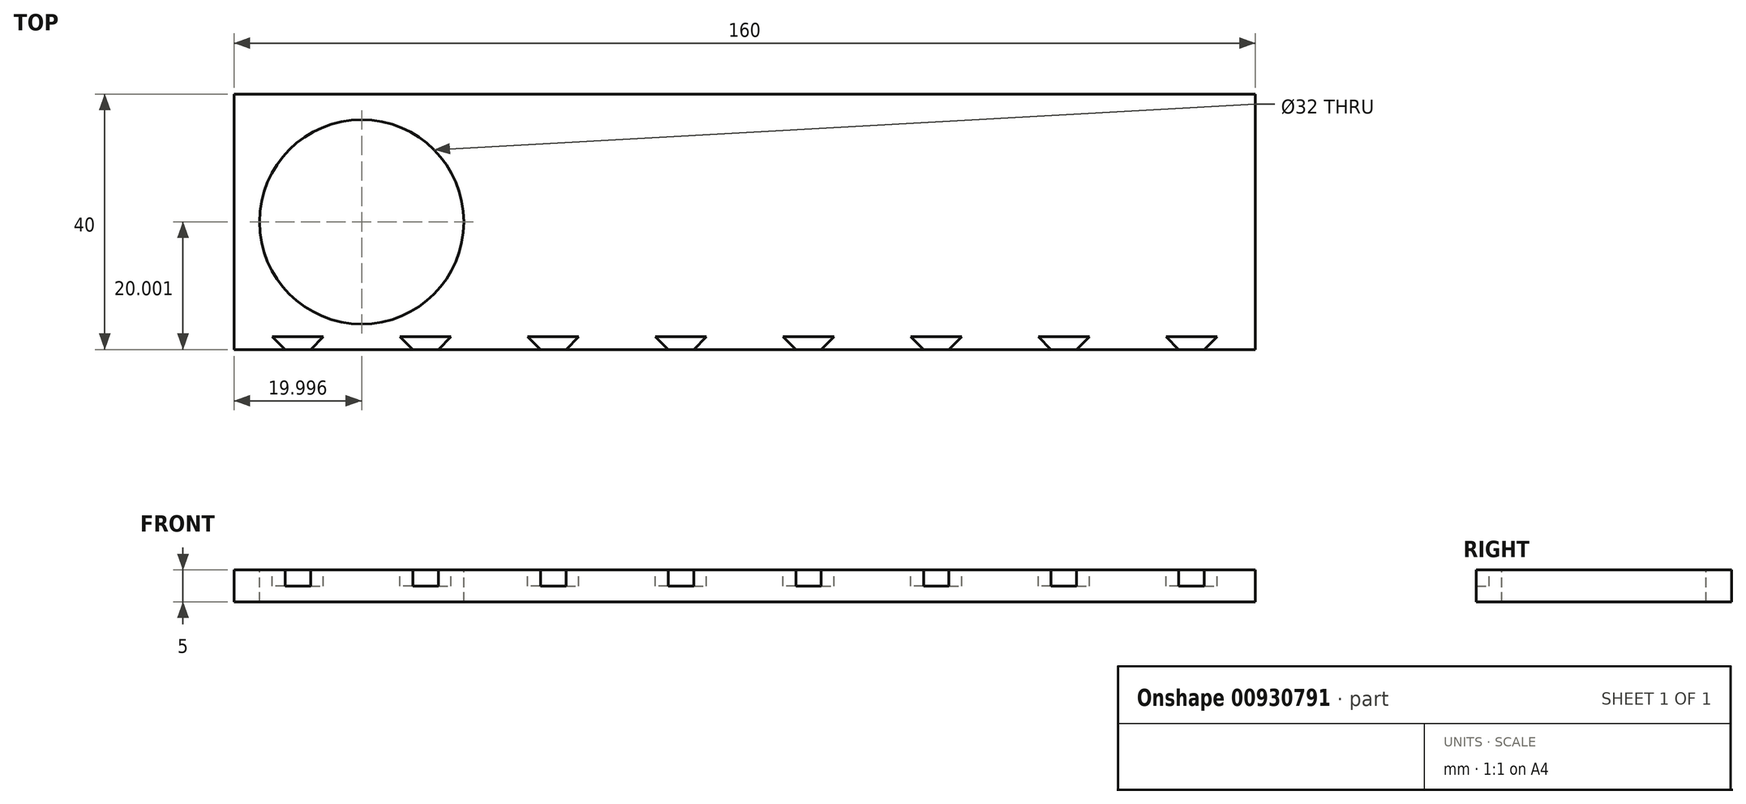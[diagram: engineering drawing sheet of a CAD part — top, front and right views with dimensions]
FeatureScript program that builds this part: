
annotation { "Feature Type Name" : "Feature", "Feature Type Description" : "" }
export const myFeature = defineFeature(function(context is Context, id is Id, definition is map)
    precondition{}
    {
        {
            var Q0;
            Q0=qCreatedBy(makeId("Top.planeOp"),FACE);
            var sketch = newSketch(context, id + "F0", { "sketchPlane" : qUnion([Q0])});
            skLineSegment(sketch, "E0.bottom", {"start": v(-67.6, 58.98) * mm, "end": v(92.4, 58.98) * mm});
            skLineSegment(sketch, "E0.top", {"start": v(-67.6, 18.98) * mm, "end": v(92.4, 18.98) * mm});
            skLineSegment(sketch, "E0.left", {"start": v(-67.6, 58.98) * mm, "end": v(-67.6, 18.98) * mm});
            skLineSegment(sketch, "E0.right", {"start": v(92.4, 58.98) * mm, "end": v(92.4, 18.98) * mm});
            skSolve(sketch);
        }
        {
            var Q0;
            Q0=makeQuery(id+"F0.imprint","IMPRINT",FACE,{"disambiguationData":[TD([[makeQuery(id+"F0.imprint","IMPRINT",EDGE,{"derivedFrom":sQuery(id+"F0.wireOp",EDGE,"E0.bottom")}),-1.0]])]});
            extrude(context, id + "F1", {"entities" : qUnion([Q0]), "depth" : 5 * mm, "offsetDistance" : 25 * mm});
        }
        {
            var Q0;
            Q0=makeQuery(id+"F1.opExtrude","CAP_FACE",FACE,{"disambiguationData":[OSD([sQuery(id+"F0.wireOp",EDGE,"E0.bottom"),sQuery(id+"F0.wireOp",EDGE,"E0.top"),sQuery(id+"F0.wireOp",EDGE,"E0.left"),sQuery(id+"F0.wireOp",EDGE,"E0.right")])],"isStart":false});
            var sketch = newSketch(context, id + "F2", { "sketchPlane" : qUnion([Q0])});
            skCircle(sketch, "E1", {"center": v(-47.6, 38.98) * mm, "radius": 16 * mm});
            skPoint(sketch, "E1.centerSnap0", {"position": v(-67.6, 38.98) * mm});
            skSolve(sketch);
        }
        {
            var Q0;
            Q0=makeQuery(id+"F2.imprint","IMPRINT",FACE,{"disambiguationData":[TD([[makeQuery(id+"F2.imprint","IMPRINT",EDGE,{"derivedFrom":sQuery(id+"F2.wireOp",EDGE,"E1")}),1.0]])]});
            extrude(context, id + "F3", {"entities" : qUnion([Q0]), "operationType" : NewBodyOperationType.REMOVE, "oppositeDirection" : true, "depth" : 5 * mm, "offsetDistance" : 25 * mm});
        }
        {
            var Q0;
            Q0=makeQuery(id+"F1.opExtrude","CAP_FACE",FACE,{"disambiguationData":[OSD([sQuery(id+"F0.wireOp",EDGE,"E0.bottom"),sQuery(id+"F0.wireOp",EDGE,"E0.top"),sQuery(id+"F0.wireOp",EDGE,"E0.left"),sQuery(id+"F0.wireOp",EDGE,"E0.right")])],"isStart":false});
            var sketch = newSketch(context, id + "F4", { "sketchPlane" : qUnion([Q0])});
            skLineSegment(sketch, "E2", {"start": v(-67.6, 20.98) * mm, "end": v(92.4, 20.98) * mm});
            skPoint(sketch, "E3", {"position": v(-57.6, 18.98) * mm});
            skLineSegment(sketch, "E4", {"start": v(-59.6, 18.98) * mm, "end": v(-61.6, 20.98) * mm});
            skLineSegment(sketch, "E5", {"start": v(-55.6, 18.98) * mm, "end": v(-53.6, 20.98) * mm});
            skLineSegment(sketch, "E6.1.0.0", {"start": v(-39.6, 18.98) * mm, "end": v(-41.6, 20.98) * mm});
            skLineSegment(sketch, "E6.1.0.1", {"start": v(-35.6, 18.98) * mm, "end": v(-33.6, 20.98) * mm});
            skPoint(sketch, "E6.1.0.2", {"position": v(-37.6, 18.98) * mm});
            skLineSegment(sketch, "E6.2.0.0", {"start": v(-19.6, 18.98) * mm, "end": v(-21.6, 20.98) * mm});
            skLineSegment(sketch, "E6.2.0.1", {"start": v(-15.6, 18.98) * mm, "end": v(-13.6, 20.98) * mm});
            skPoint(sketch, "E6.2.0.2", {"position": v(-17.6, 18.98) * mm});
            skLineSegment(sketch, "E6.3.0.0", {"start": v(0.4, 18.98) * mm, "end": v(-1.6, 20.98) * mm});
            skLineSegment(sketch, "E6.3.0.1", {"start": v(4.4, 18.98) * mm, "end": v(6.4, 20.98) * mm});
            skPoint(sketch, "E6.3.0.2", {"position": v(2.4, 18.98) * mm});
            skLineSegment(sketch, "E6.4.0.0", {"start": v(20.4, 18.98) * mm, "end": v(18.4, 20.98) * mm});
            skLineSegment(sketch, "E6.4.0.1", {"start": v(24.4, 18.98) * mm, "end": v(26.4, 20.98) * mm});
            skPoint(sketch, "E6.4.0.2", {"position": v(22.4, 18.98) * mm});
            skLineSegment(sketch, "E6.5.0.0", {"start": v(40.4, 18.98) * mm, "end": v(38.4, 20.98) * mm});
            skLineSegment(sketch, "E6.5.0.1", {"start": v(44.4, 18.98) * mm, "end": v(46.4, 20.98) * mm});
            skPoint(sketch, "E6.5.0.2", {"position": v(42.4, 18.98) * mm});
            skLineSegment(sketch, "E6.6.0.0", {"start": v(60.4, 18.98) * mm, "end": v(58.4, 20.98) * mm});
            skLineSegment(sketch, "E6.6.0.1", {"start": v(64.4, 18.98) * mm, "end": v(66.4, 20.98) * mm});
            skPoint(sketch, "E6.6.0.2", {"position": v(62.4, 18.98) * mm});
            skLineSegment(sketch, "E6.7.0.0", {"start": v(80.4, 18.98) * mm, "end": v(78.4, 20.98) * mm});
            skLineSegment(sketch, "E6.7.0.1", {"start": v(84.4, 18.98) * mm, "end": v(86.4, 20.98) * mm});
            skPoint(sketch, "E6.7.0.2", {"position": v(82.4, 18.98) * mm});
            skLineSegment(sketch, "E6.direction1", {"start": v(-59.6, 18.98) * mm, "end": v(-39.6, 18.98) * mm, "construction": true});
            skSolve(sketch);
        }
        {
            var Q0;
            {var subQ0=sQuery(id+"F4.wireOp",EDGE,"E4");Q0=makeQuery(id+"F4.imprint","IMPRINT",FACE,{"disambiguationData":[TD([[makeQuery(id+"F4.imprint","IMPRINT",EDGE,{"derivedFrom":subQ0}),-1.0]])]});}
            var Q1;
            {var subQ0=sQuery(id+"F4.wireOp",EDGE,"E6.1.0.0");Q1=makeQuery(id+"F4.imprint","IMPRINT",FACE,{"disambiguationData":[TD([[makeQuery(id+"F4.imprint","IMPRINT",EDGE,{"derivedFrom":subQ0}),-1.0]])]});}
            var Q2;
            {var subQ0=sQuery(id+"F4.wireOp",EDGE,"E6.2.0.0");Q2=makeQuery(id+"F4.imprint","IMPRINT",FACE,{"disambiguationData":[TD([[makeQuery(id+"F4.imprint","IMPRINT",EDGE,{"derivedFrom":subQ0}),-1.0]])]});}
            var Q3;
            {var subQ0=sQuery(id+"F4.wireOp",EDGE,"E6.3.0.0");Q3=makeQuery(id+"F4.imprint","IMPRINT",FACE,{"disambiguationData":[TD([[makeQuery(id+"F4.imprint","IMPRINT",EDGE,{"derivedFrom":subQ0}),-1.0]])]});}
            var Q4;
            {var subQ0=sQuery(id+"F4.wireOp",EDGE,"E6.4.0.0");Q4=makeQuery(id+"F4.imprint","IMPRINT",FACE,{"disambiguationData":[TD([[makeQuery(id+"F4.imprint","IMPRINT",EDGE,{"derivedFrom":subQ0}),-1.0]])]});}
            var Q5;
            {var subQ0=sQuery(id+"F4.wireOp",EDGE,"E6.5.0.0");Q5=makeQuery(id+"F4.imprint","IMPRINT",FACE,{"disambiguationData":[TD([[makeQuery(id+"F4.imprint","IMPRINT",EDGE,{"derivedFrom":subQ0}),-1.0]])]});}
            var Q6;
            {var subQ0=sQuery(id+"F4.wireOp",EDGE,"E6.6.0.0");Q6=makeQuery(id+"F4.imprint","IMPRINT",FACE,{"disambiguationData":[TD([[makeQuery(id+"F4.imprint","IMPRINT",EDGE,{"derivedFrom":subQ0}),-1.0]])]});}
            var Q7;
            {var subQ0=sQuery(id+"F4.wireOp",EDGE,"E6.7.0.0");Q7=makeQuery(id+"F4.imprint","IMPRINT",FACE,{"disambiguationData":[TD([[makeQuery(id+"F4.imprint","IMPRINT",EDGE,{"derivedFrom":subQ0}),-1.0]])]});}
            extrude(context, id + "F5", {"entities" : qUnion([Q0, Q1, Q2, Q3, Q4, Q5, Q6, Q7]), "operationType" : NewBodyOperationType.REMOVE, "oppositeDirection" : true, "depth" : 2.5 * mm, "offsetDistance" : 25 * mm});
        }
    });
